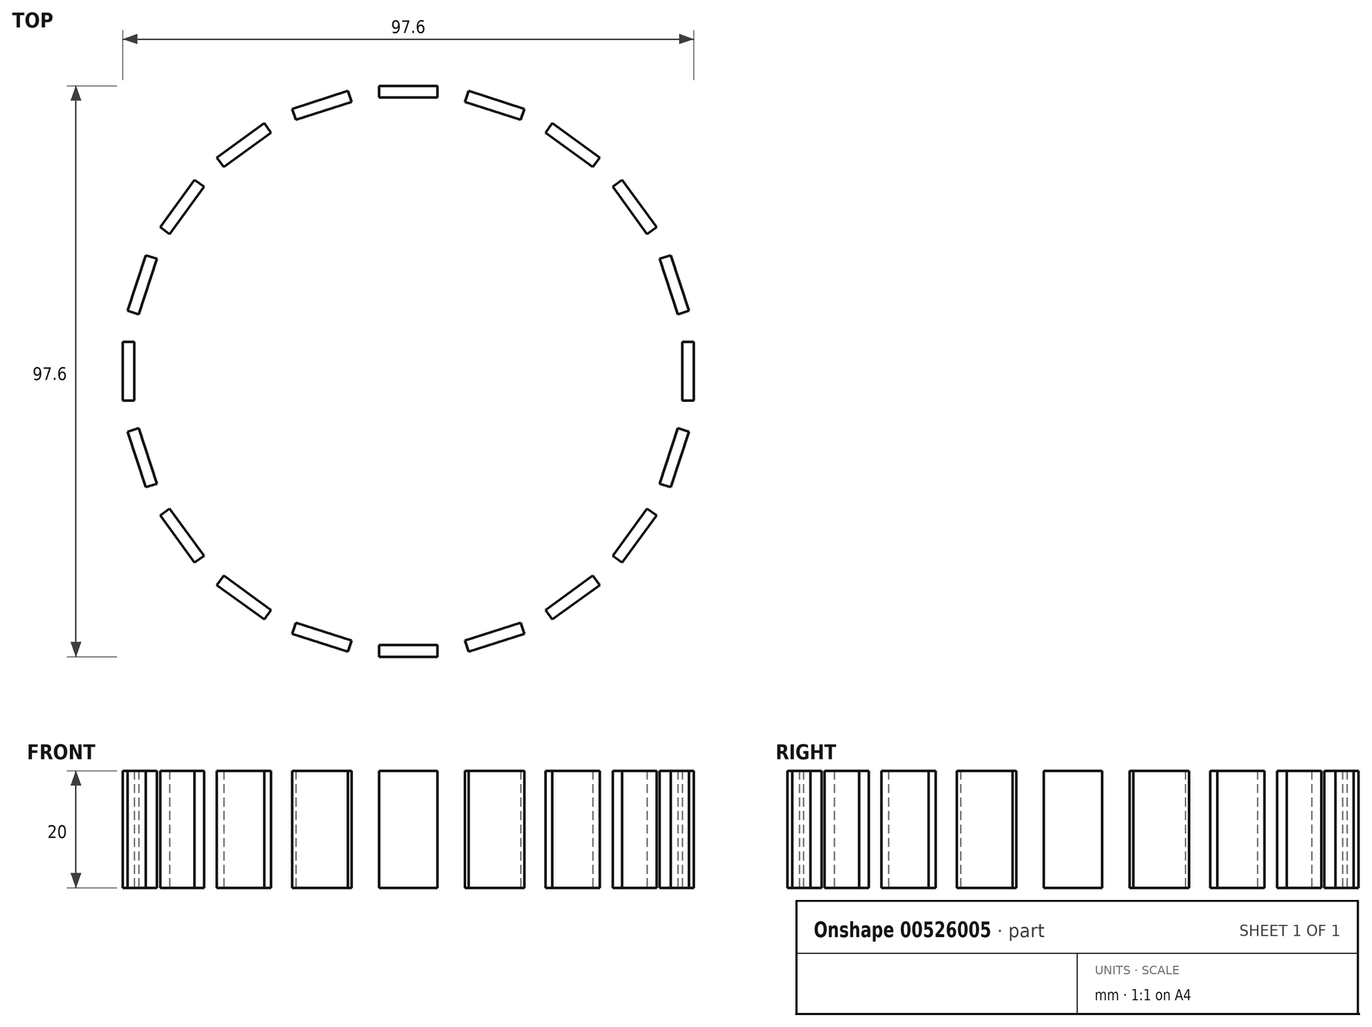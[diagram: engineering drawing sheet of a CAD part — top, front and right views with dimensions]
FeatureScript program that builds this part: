
annotation { "Feature Type Name" : "Feature", "Feature Type Description" : "" }
export const myFeature = defineFeature(function(context is Context, id is Id, definition is map)
    precondition{}
    {
        {
            var Q0;
            Q0=qCreatedBy(makeId("Right.planeOp"),FACE);
            cPlane(context, id + "F0", {"entities" : qUnion([Q0]), "cplaneType" : CPlaneType.OFFSET, "offset" : 48.8 * mm, "width" : 150 * mm, "height" : 150 * mm});
        }
        {
            var Q0;
            Q0=qCreatedBy(id+"F0.planeOp",FACE);
            var sketch = newSketch(context, id + "F1", { "sketchPlane" : qUnion([Q0])});
            skLineSegment(sketch, "E0.bottom", {"start": v(-5, 0) * mm, "end": v(5, 0) * mm});
            skLineSegment(sketch, "E0.top", {"start": v(-5, -20) * mm, "end": v(5, -20) * mm});
            skLineSegment(sketch, "E0.left", {"start": v(-5, 0) * mm, "end": v(-5, -20) * mm});
            skLineSegment(sketch, "E0.right", {"start": v(5, 0) * mm, "end": v(5, -20) * mm});
            skSolve(sketch);
        }
        {
            var Q0;
            Q0=qSketchRegion(id+"F1",true);
            extrude(context, id + "F2", {"entities" : qUnion([Q0]), "oppositeDirection" : true, "depth" : 2 * mm});
        }
        {
            var Q0;
            Q0=qCreatedBy(makeId("Right.planeOp"),FACE);
            var sketch = newSketch(context, id + "F3", { "sketchPlane" : qUnion([Q0])});
            skLineSegment(sketch, "E1", {"start": v(0, -68.8) * mm, "end": v(0, 63.41) * mm, "construction": true});
            skSolve(sketch);
        }
        {
            var Q0;
            Q0=makeQuery(id+"F2.opExtrude","SWEPT_BODY",BODY,{"disambiguationData":[OSD([sQuery(id+"F1.wireOp",EDGE,"E0.bottom"),sQuery(id+"F1.wireOp",EDGE,"E0.top"),sQuery(id+"F1.wireOp",EDGE,"E0.left"),sQuery(id+"F1.wireOp",EDGE,"E0.right")])]});
            var Q1;
            Q1=sQuery(id+"F3.wireOp",EDGE,"E1");
            circularPattern(context, id + "F4", {"operationType" : NewBodyOperationType.ADD, "entities" : qUnion([Q0]), "axis" : qUnion([Q1]), "angle" : 360 * degree, "instanceCount" : 20, "equalSpace" : true});
        }
    });
